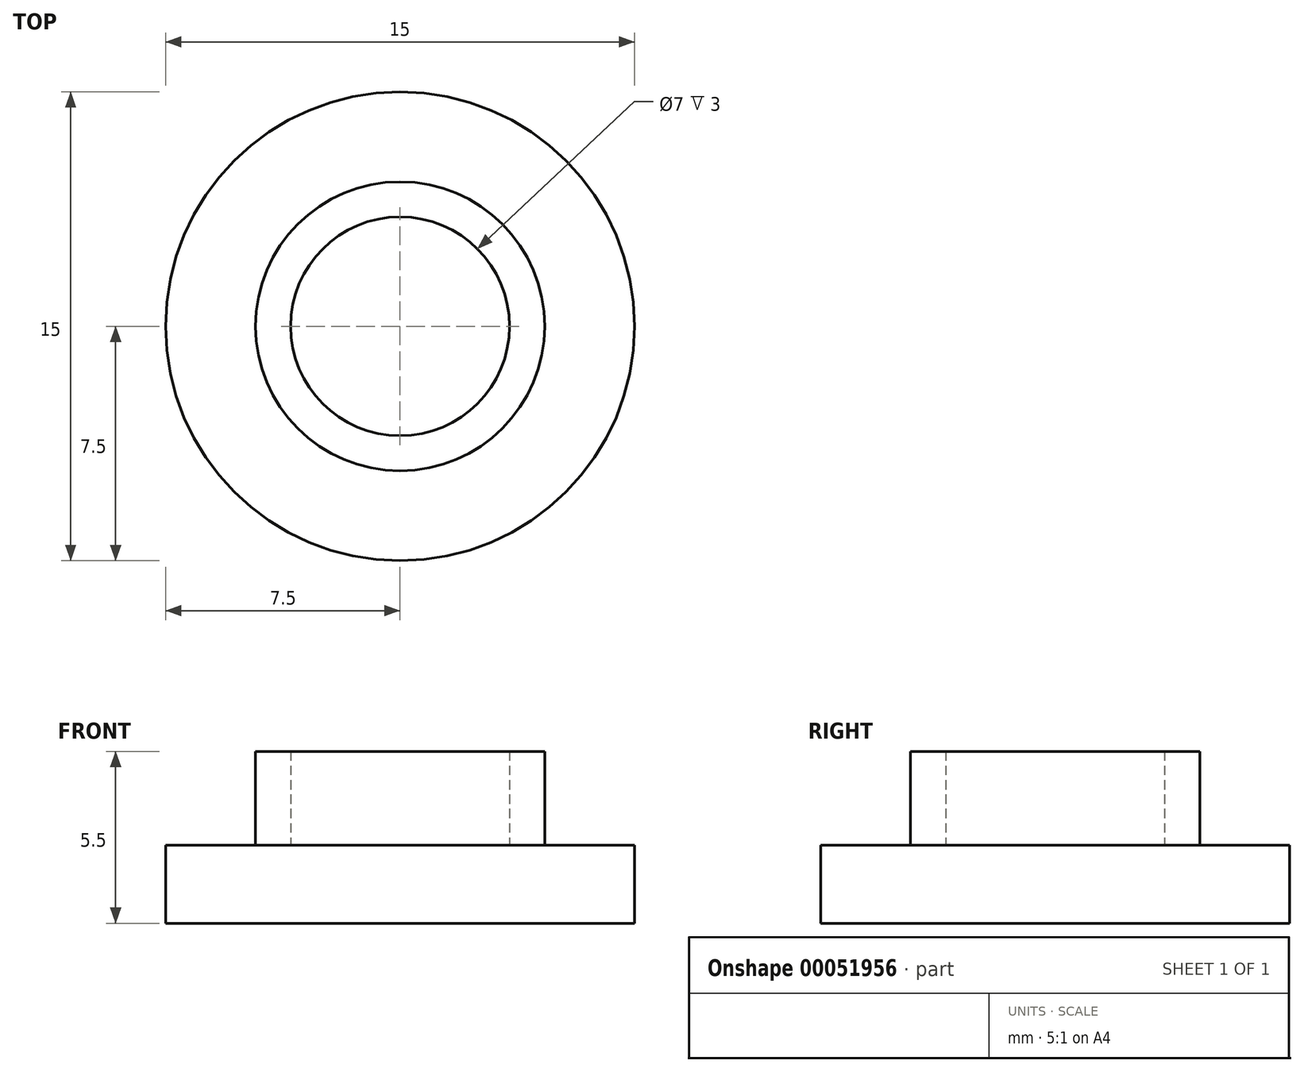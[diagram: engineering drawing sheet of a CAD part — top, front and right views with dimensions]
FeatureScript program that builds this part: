
annotation { "Feature Type Name" : "Feature", "Feature Type Description" : "" }
export const myFeature = defineFeature(function(context is Context, id is Id, definition is map)
    precondition{}
    {
        {
            var Q0;
            Q0=qCreatedBy(makeId("Top.planeOp"),FACE);
            var sketch = newSketch(context, id + "F0", { "sketchPlane" : qUnion([Q0])});
            skCircle(sketch, "E0", {"center": v(0, 0) * mm, "radius": 4.62 * mm});
            skCircle(sketch, "E1", {"center": v(0, 0) * mm, "radius": 7.5 * mm});
            skCircle(sketch, "E2", {"center": v(0, 0) * mm, "radius": 3.5 * mm});
            skSolve(sketch);
        }
        {
            var Q0;
            Q0=makeQuery(id+"F0.imprint","IMPRINT",FACE,{"disambiguationData":[TD([[makeQuery(id+"F0.imprint","IMPRINT",EDGE,{"derivedFrom":sQuery(id+"F0.wireOp",EDGE,"E0")}),-1.0]])]});
            var Q1;
            Q1=makeQuery(id+"F0.imprint","IMPRINT",FACE,{"disambiguationData":[TD([[makeQuery(id+"F0.imprint","IMPRINT",EDGE,{"derivedFrom":sQuery(id+"F0.wireOp",EDGE,"E0")}),1.0]])]});
            var Q2;
            Q2=makeQuery(id+"F0.imprint","IMPRINT",FACE,{"disambiguationData":[TD([[makeQuery(id+"F0.imprint","IMPRINT",EDGE,{"derivedFrom":sQuery(id+"F0.wireOp",EDGE,"E2")}),1.0]])]});
            extrude(context, id + "F1", {"entities" : qUnion([Q0, Q1, Q2]), "oppositeDirection" : true, "depth" : 2.5 * mm});
        }
        {
            var Q0;
            Q0=makeQuery(id+"F0.imprint","IMPRINT",FACE,{"disambiguationData":[TD([[makeQuery(id+"F0.imprint","IMPRINT",EDGE,{"derivedFrom":sQuery(id+"F0.wireOp",EDGE,"E0")}),1.0]])]});
            extrude(context, id + "F2", {"entities" : qUnion([Q0]), "operationType" : NewBodyOperationType.ADD, "depth" : 3 * mm});
        }
    });
